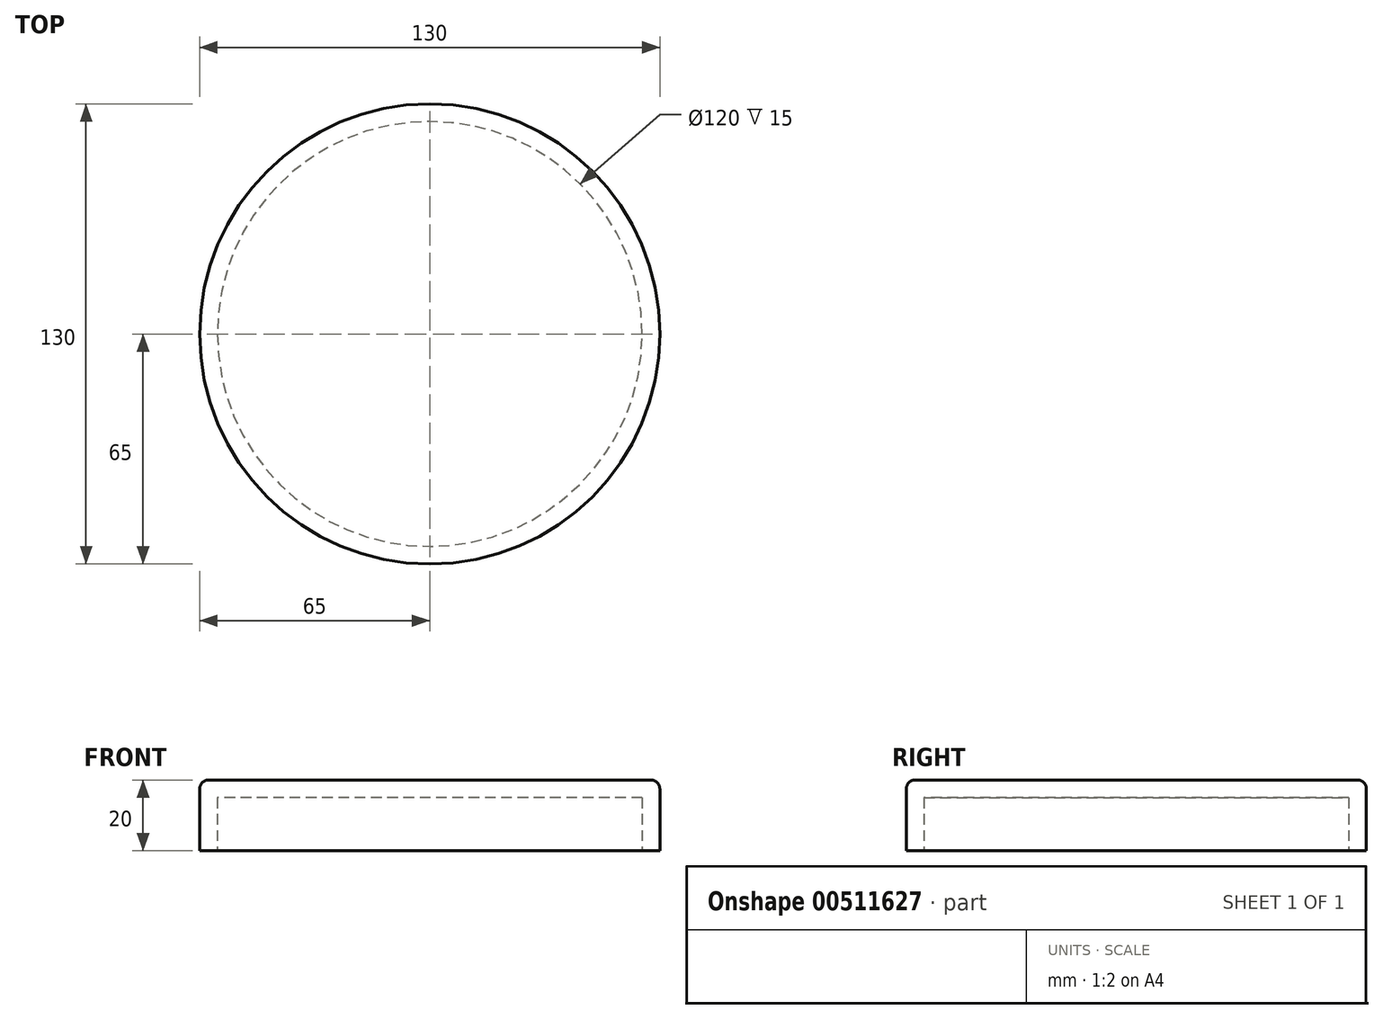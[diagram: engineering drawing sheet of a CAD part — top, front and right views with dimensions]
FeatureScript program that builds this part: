
annotation { "Feature Type Name" : "Feature", "Feature Type Description" : "" }
export const myFeature = defineFeature(function(context is Context, id is Id, definition is map)
    precondition{}
    {
        {
            var Q0;
            Q0=qCreatedBy(makeId("Top.planeOp"),FACE);
            var sketch = newSketch(context, id + "F0", { "sketchPlane" : qUnion([Q0])});
            skCircle(sketch, "E0", {"center": v(0, 0) * mm, "radius": 65 * mm});
            skSolve(sketch);
        }
        {
            var Q0;
            Q0=makeQuery(id+"F0.imprint","IMPRINT",FACE,{"disambiguationData":[TD([[makeQuery(id+"F0.imprint","IMPRINT",EDGE,{"derivedFrom":sQuery(id+"F0.wireOp",EDGE,"E0")}),1.0]])]});
            extrude(context, id + "F1", {"entities" : qUnion([Q0]), "depth" : 20 * mm});
        }
        {
            var Q0;
            Q0=makeQuery(id+"F1.opExtrude","CAP_FACE",FACE,{"disambiguationData":[OSD([sQuery(id+"F0.wireOp",EDGE,"E0")])],"isStart":true});
            shell(context, id + "F2", {"entities" : qUnion([Q0]), "thickness" : 5 * mm});
        }
        {
            var Q0;
            Q0=makeQuery(id+"F1.opExtrude","CAP_EDGE",EDGE,{"disambiguationData":[OSD([sQuery(id+"F0.wireOp",EDGE,"E0")])],"isStart":false});
            fillet(context, id + "F3", {"entities" : qUnion([Q0]), "radius" : 2.5 * mm, "tangentPropagation" : true, "allowEdgeOverflow" : false});
        }
    });
